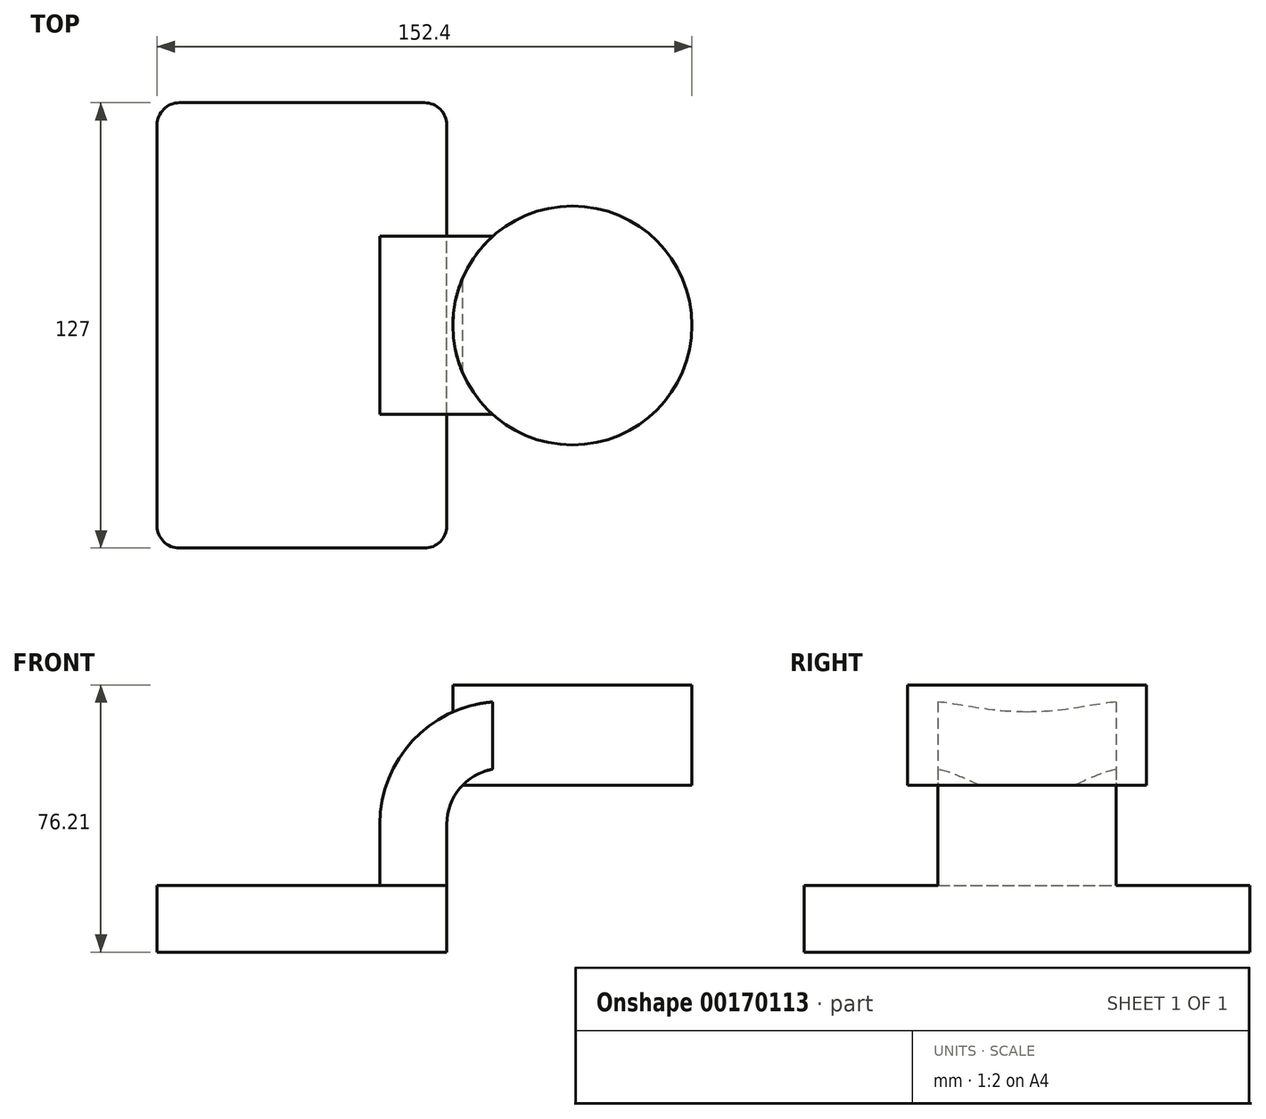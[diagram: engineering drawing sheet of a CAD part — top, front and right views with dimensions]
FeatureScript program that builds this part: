
annotation { "Feature Type Name" : "Feature", "Feature Type Description" : "" }
export const myFeature = defineFeature(function(context is Context, id is Id, definition is map)
    precondition{}
    {
        {
            var Q0;
            Q0=qCreatedBy(makeId("Front.planeOp"),FACE);
            var sketch = newSketch(context, id + "F0", { "sketchPlane" : qUnion([Q0])});
            skLineSegment(sketch, "E0.bottom", {"start": v(41.27, 9.53) * mm, "end": v(-41.28, 9.53) * mm});
            skLineSegment(sketch, "E0.top", {"start": v(41.28, -9.52) * mm, "end": v(-41.27, -9.52) * mm});
            skLineSegment(sketch, "E0.left", {"start": v(41.28, 9.53) * mm, "end": v(41.28, -9.52) * mm});
            skLineSegment(sketch, "E0.right", {"start": v(-41.28, 9.52) * mm, "end": v(-41.27, -9.52) * mm});
            skPoint(sketch, "E0.middle", {"position": v(0, 0) * mm});
            skLineSegment(sketch, "E1.bottom", {"start": v(111.12, 66.68) * mm, "end": v(60.32, 66.68) * mm});
            skLineSegment(sketch, "E1.top", {"start": v(111.12, 38.1) * mm, "end": v(60.32, 38.1) * mm});
            skLineSegment(sketch, "E1.left", {"start": v(111.12, 66.68) * mm, "end": v(111.12, 38.1) * mm});
            skLineSegment(sketch, "E1.right", {"start": v(60.32, 66.68) * mm, "end": v(60.32, 38.1) * mm});
            skPoint(sketch, "E1.middle", {"position": v(85.72, 52.39) * mm});
            skLineSegment(sketch, "E2", {"start": v(41.27, 9.53) * mm, "end": v(41.27, 27) * mm});
            skArc(sketch, "E3", {"start": v(41.28, 27) * mm, "mid": v(45.92, 38.23) * mm, "end": v(57.15, 42.88) * mm});
            skLineSegment(sketch, "E4", {"start": v(57.15, 42.88) * mm, "end": v(77.06, 42.88) * mm});
            skLineSegment(sketch, "E5.0", {"start": v(57.15, 61.93) * mm, "end": v(77.06, 61.93) * mm});
            skArc(sketch, "E5.1", {"start": v(22.23, 27) * mm, "mid": v(32.45, 51.7) * mm, "end": v(57.15, 61.93) * mm});
            skLineSegment(sketch, "E5.2", {"start": v(22.23, 9.53) * mm, "end": v(22.23, 27) * mm});
            skLineSegment(sketch, "E6", {"start": v(77.06, 38.1) * mm, "end": v(77.06, 66.68) * mm});
            skFitSpline(sketch, "E7", {"points": [v(-41.28, 9.52) * mm, v(57.15, 61.93) * mm], "startDerivative": vector(0, 42.6) * mm, "endDerivative": vector(198.78, 0) * mm});
            skSolve(sketch);
        }
        {
            var Q0;
            Q0=makeQuery(id+"F0.imprint","IMPRINT",FACE,{"disambiguationData":[TD([[makeQuery(id+"F0.imprint","IMPRINT",EDGE,{"derivedFrom":sQuery(id+"F0.wireOp",EDGE,"E0.top")}),-1.0]])]});
            extrude(context, id + "F1", {"entities" : qUnion([Q0]), "endBound" : BoundingType.SYMMETRIC, "depth" : 127 * mm});
        }
        {
            var Q0;
            {var subQ0=sQuery(id+"F0.wireOp",EDGE,"E5.0");var subQ1=sQuery(id+"F0.wireOp",EDGE,"E1.right");var subQ2=makeQuery(id+"F0.imprint","INTERSECT",VERTEX,{"derivedFrom":[subQ1,subQ0]});Q0=makeQuery(id+"F0.imprint","IMPRINT",FACE,{"disambiguationData":[TD([[makeQuery(id+"F0.imprint","IMPRINT",EDGE,{"disambiguationData":[TD([[subQ2,-1.0]])],"derivedFrom":subQ1}),1.0]])]});}
            var Q1;
            {var subQ1=sQuery(id+"F0.wireOp",EDGE,"E2");Q1=makeQuery(id+"F0.imprint","IMPRINT",FACE,{"disambiguationData":[TD([[makeQuery(id+"F0.imprint","IMPRINT",EDGE,{"derivedFrom":subQ1}),1.0]])]});}
            extrude(context, id + "F2", {"entities" : qUnion([Q0, Q1]), "operationType" : NewBodyOperationType.ADD, "endBound" : BoundingType.SYMMETRIC, "depth" : 50.8 * mm});
        }
        {
            var Q0;
            Q0=makeQuery(id+"F0.imprint","IMPRINT",FACE,{"disambiguationData":[TD([[makeQuery(id+"F0.imprint","IMPRINT",EDGE,{"derivedFrom":sQuery(id+"F0.wireOp",EDGE,"E5.1")}),1.0]])]});
            extrude(context, id + "F3", {"entities" : qUnion([Q0]), "operationType" : NewBodyOperationType.ADD, "endBound" : BoundingType.SYMMETRIC, "depth" : 15.88 * mm});
        }
        {
            var Q0;
            {var subQ0=sQuery(id+"F0.wireOp",EDGE,"E1.left");Q0=makeQuery(id+"F0.imprint","IMPRINT",FACE,{"disambiguationData":[TD([[makeQuery(id+"F0.imprint","IMPRINT",EDGE,{"derivedFrom":subQ0}),-1.0]])]});}
            var Q1;
            Q1=sQuery(id+"F0.wireOp",EDGE,"E6");
            revolve(context, id + "F4", {"operationType" : NewBodyOperationType.ADD, "entities" : qUnion([Q0]), "axis" : qUnion([Q1]), "revolveType" : RevolveType.FULL});
        }
        {
            var Q0;
            Q0=makeQuery(id+"F1.opExtrude","CAP_EDGE",EDGE,{"disambiguationData":[OSD([sQuery(id+"F0.wireOp",EDGE,"E0.left")])],"isStart":false});
            var Q1;
            Q1=makeQuery(id+"F1.opExtrude","CAP_EDGE",EDGE,{"disambiguationData":[OSD([sQuery(id+"F0.wireOp",EDGE,"E0.right")])],"isStart":false});
            var Q2;
            Q2=makeQuery(id+"F1.opExtrude","CAP_EDGE",EDGE,{"disambiguationData":[OSD([sQuery(id+"F0.wireOp",EDGE,"E0.right")])],"isStart":true});
            var Q3;
            Q3=makeQuery(id+"F1.opExtrude","CAP_EDGE",EDGE,{"disambiguationData":[OSD([sQuery(id+"F0.wireOp",EDGE,"E0.left")])],"isStart":true});
            fillet(context, id + "F5", {"entities" : qUnion([Q0, Q1, Q2, Q3]), "radius" : 6.35 * mm, "tangentPropagation" : true, "allowEdgeOverflow" : false});
        }
    });
